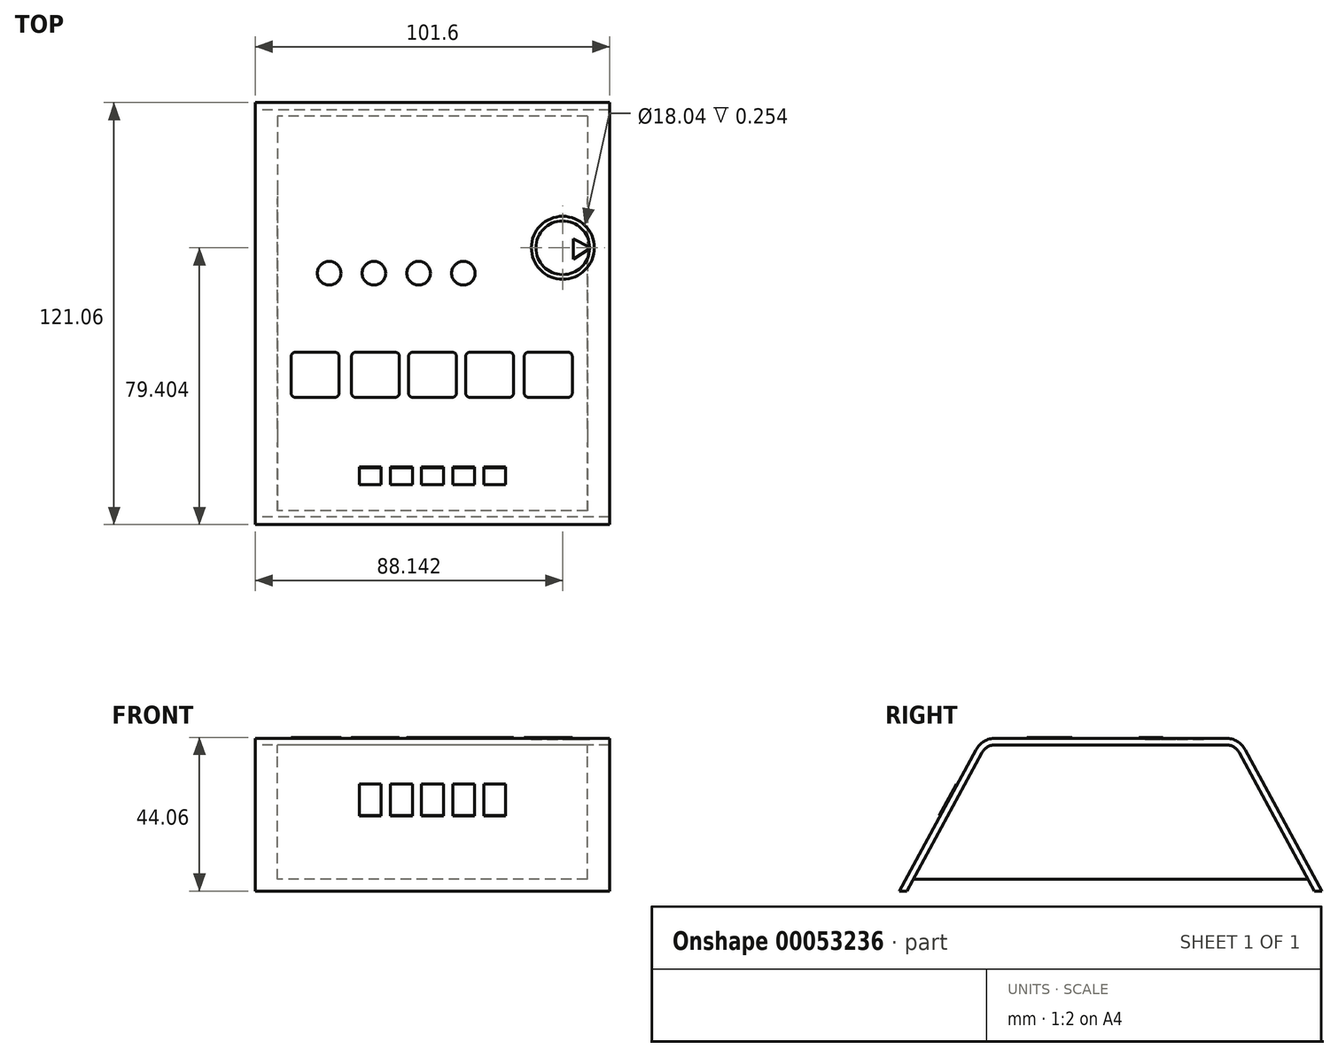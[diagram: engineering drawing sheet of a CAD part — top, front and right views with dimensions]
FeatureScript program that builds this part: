
annotation { "Feature Type Name" : "Feature", "Feature Type Description" : "" }
export const myFeature = defineFeature(function(context is Context, id is Id, definition is map)
    precondition{}
    {
        {
            var Q0;
            Q0=qCreatedBy(makeId("Top.planeOp"),FACE);
            var sketch = newSketch(context, id + "F0", { "sketchPlane" : qUnion([Q0])});
            skLineSegment(sketch, "E0.bottom", {"start": v(-38, 33) * mm, "end": v(38, 33) * mm});
            skLineSegment(sketch, "E0.top", {"start": v(-38, -33) * mm, "end": v(38, -33) * mm});
            skLineSegment(sketch, "E0.left", {"start": v(-38, 33) * mm, "end": v(-38, -33) * mm});
            skLineSegment(sketch, "E0.right", {"start": v(38, 33) * mm, "end": v(38, -33) * mm});
            skLineSegment(sketch, "E1", {"start": v(0, 33) * mm, "end": v(0, -33) * mm, "construction": true});
            skLineSegment(sketch, "E2", {"start": v(-38, 0) * mm, "end": v(38, 0) * mm, "construction": true});
            skSolve(sketch);
        }
        {
            var Q0;
            Q0=qCreatedBy(makeId("Right.planeOp"),FACE);
            var sketch = newSketch(context, id + "F1", { "sketchPlane" : qUnion([Q0])});
            skLineSegment(sketch, "E3", {"start": v(-60.53, -28.5) * mm, "end": v(-38.6, 11.98) * mm});
            skLineSegment(sketch, "E4", {"start": v(-33.02, 15.3) * mm, "end": v(0, 15.3) * mm});
            skPoint(sketch, "E5.visualSharp", {"position": v(-36.8, 15.3) * mm});
            skArc(sketch, "E5.filletArc", {"start": v(-33.02, 15.3) * mm, "mid": v(-36.27, 14.41) * mm, "end": v(-38.6, 11.98) * mm});
            skLineSegment(sketch, "E6.0", {"start": v(-33.02, 13.42) * mm, "end": v(7.41, 13.42) * mm});
            skArc(sketch, "E6.1", {"start": v(-33.02, 13.42) * mm, "mid": v(-35.3, 12.8) * mm, "end": v(-36.95, 11.08) * mm});
            skLineSegment(sketch, "E6.2", {"start": v(-58.39, -28.5) * mm, "end": v(-36.95, 11.08) * mm});
            skLineSegment(sketch, "E7", {"start": v(-60.53, -28.5) * mm, "end": v(-58.39, -28.5) * mm});
            skLineSegment(sketch, "E8.MirrorCS", {"start": v(33.02, 15.3) * mm, "end": v(0, 15.3) * mm});
            skLineSegment(sketch, "E9.MirrorCS", {"start": v(33.02, 13.42) * mm, "end": v(-7.41, 13.42) * mm});
            skArc(sketch, "E10.MirrorCS", {"start": v(33.02, 13.42) * mm, "mid": v(35.3, 12.8) * mm, "end": v(36.95, 11.08) * mm});
            skArc(sketch, "E11.MirrorCS", {"start": v(33.02, 15.3) * mm, "mid": v(36.27, 14.41) * mm, "end": v(38.6, 11.98) * mm});
            skLineSegment(sketch, "E12.MirrorCS", {"start": v(60.53, -28.5) * mm, "end": v(38.6, 11.98) * mm});
            skLineSegment(sketch, "E13.MirrorCS", {"start": v(58.39, -28.5) * mm, "end": v(36.95, 11.08) * mm});
            skLineSegment(sketch, "E14.MirrorCS", {"start": v(60.53, -28.5) * mm, "end": v(58.39, -28.5) * mm});
            skSolve(sketch);
        }
        {
            var Q0;
            Q0=makeQuery(id+"F1.imprint","IMPRINT",FACE,{"disambiguationData":[TD([[makeQuery(id+"F1.imprint","IMPRINT",EDGE,{"derivedFrom":sQuery(id+"F1.wireOp",EDGE,"E3")}),-1.0]])]});
            extrude(context, id + "F2", {"entities" : qUnion([Q0]), "endBound" : BoundingType.SYMMETRIC, "depth" : 101.6 * mm});
        }
        {
            var Q0;
            Q0 = qConstructionFilter(qBodyType(qCreatedBy(id + "F0" ,EDGE), BodyType.WIRE), ConstructionObject.NO);
            extrude(context, id + "F3", {"bodyType" : ToolBodyType.SURFACE, "surfaceEntities" : qUnion([Q0]), "oppositeDirection" : true, "depth" : 19 * mm});
        }
        {
            var Q0;
            Q0=makeQuery(id+"F2.opExtrude","SWEPT_FACE",FACE,{"disambiguationData":[OSD([sQuery(id+"F1.wireOp",EDGE,"E3")])]});
            var sketch = newSketch(context, id + "F4", { "sketchPlane" : qUnion([Q0])});
            skLineSegment(sketch, "E15.bottom", {"start": v(-21, -19.14) * mm, "end": v(-14.72, -19.14) * mm});
            skLineSegment(sketch, "E15.top", {"start": v(-21, -29.42) * mm, "end": v(-14.72, -29.42) * mm});
            skLineSegment(sketch, "E15.left", {"start": v(-21, -19.14) * mm, "end": v(-21, -29.42) * mm});
            skLineSegment(sketch, "E15.right", {"start": v(-14.72, -19.14) * mm, "end": v(-14.72, -29.42) * mm});
            skLineSegment(sketch, "E16.bottom", {"start": v(-12.07, -19.14) * mm, "end": v(-5.79, -19.14) * mm});
            skLineSegment(sketch, "E16.top", {"start": v(-12.07, -29.42) * mm, "end": v(-5.79, -29.42) * mm});
            skLineSegment(sketch, "E16.left", {"start": v(-12.07, -19.14) * mm, "end": v(-12.07, -29.42) * mm});
            skLineSegment(sketch, "E16.right", {"start": v(-5.79, -19.14) * mm, "end": v(-5.79, -29.42) * mm});
            skLineSegment(sketch, "E17.bottom", {"start": v(-3.14, -19.14) * mm, "end": v(3.14, -19.14) * mm});
            skLineSegment(sketch, "E17.top", {"start": v(-3.14, -29.42) * mm, "end": v(3.14, -29.42) * mm});
            skLineSegment(sketch, "E17.left", {"start": v(-3.14, -19.14) * mm, "end": v(-3.14, -29.42) * mm});
            skLineSegment(sketch, "E17.right", {"start": v(3.14, -19.14) * mm, "end": v(3.14, -29.42) * mm});
            skLineSegment(sketch, "E18.bottom", {"start": v(5.79, -19.14) * mm, "end": v(12.07, -19.14) * mm});
            skLineSegment(sketch, "E18.top", {"start": v(5.79, -29.42) * mm, "end": v(12.07, -29.42) * mm});
            skLineSegment(sketch, "E18.left", {"start": v(5.79, -19.14) * mm, "end": v(5.79, -29.42) * mm});
            skLineSegment(sketch, "E18.right", {"start": v(12.07, -19.14) * mm, "end": v(12.07, -29.42) * mm});
            skLineSegment(sketch, "E19.bottom", {"start": v(14.72, -19.14) * mm, "end": v(21, -19.14) * mm});
            skLineSegment(sketch, "E19.top", {"start": v(14.72, -29.42) * mm, "end": v(21, -29.42) * mm});
            skLineSegment(sketch, "E19.left", {"start": v(14.72, -19.14) * mm, "end": v(14.72, -29.42) * mm});
            skLineSegment(sketch, "E19.right", {"start": v(21, -19.14) * mm, "end": v(21, -29.42) * mm});
            skLineSegment(sketch, "E20", {"start": v(-14.72, -19.14) * mm, "end": v(-12.07, -19.14) * mm, "construction": true});
            skLineSegment(sketch, "E21", {"start": v(-5.79, -19.14) * mm, "end": v(-3.14, -19.14) * mm, "construction": true});
            skLineSegment(sketch, "E22", {"start": v(3.14, -19.14) * mm, "end": v(5.79, -19.14) * mm, "construction": true});
            skLineSegment(sketch, "E23", {"start": v(12.07, -19.14) * mm, "end": v(14.72, -19.14) * mm, "construction": true});
            skLineSegment(sketch, "E24", {"start": v(0, -19.14) * mm, "end": v(0, -29.42) * mm, "construction": true});
            skSolve(sketch);
        }
        {
            var Q0;
            Q0=makeQuery(id+"F4.imprint","IMPRINT",FACE,{"disambiguationData":[TD([[makeQuery(id+"F4.imprint","IMPRINT",EDGE,{"derivedFrom":sQuery(id+"F4.wireOp",EDGE,"E15.bottom")}),-1.0]])]});
            var Q1;
            Q1=makeQuery(id+"F4.imprint","IMPRINT",FACE,{"disambiguationData":[TD([[makeQuery(id+"F4.imprint","IMPRINT",EDGE,{"derivedFrom":sQuery(id+"F4.wireOp",EDGE,"E16.bottom")}),-1.0]])]});
            var Q2;
            Q2=makeQuery(id+"F4.imprint","IMPRINT",FACE,{"disambiguationData":[TD([[makeQuery(id+"F4.imprint","IMPRINT",EDGE,{"derivedFrom":sQuery(id+"F4.wireOp",EDGE,"E17.bottom")}),-1.0]])]});
            var Q3;
            Q3=makeQuery(id+"F4.imprint","IMPRINT",FACE,{"disambiguationData":[TD([[makeQuery(id+"F4.imprint","IMPRINT",EDGE,{"derivedFrom":sQuery(id+"F4.wireOp",EDGE,"E18.bottom")}),-1.0]])]});
            var Q4;
            Q4=makeQuery(id+"F4.imprint","IMPRINT",FACE,{"disambiguationData":[TD([[makeQuery(id+"F4.imprint","IMPRINT",EDGE,{"derivedFrom":sQuery(id+"F4.wireOp",EDGE,"E19.bottom")}),-1.0]])]});
            extrude(context, id + "F5", {"entities" : qUnion([Q0, Q1, Q2, Q3, Q4]), "operationType" : NewBodyOperationType.ADD, "depth" : 0.25 * mm});
        }
        {
            var Q0;
            Q0=makeQuery(id+"F2.opExtrude","SWEPT_FACE",FACE,{"disambiguationData":[OSD([sQuery(id+"F1.wireOp",EDGE,"E4"),sQuery(id+"F1.wireOp",EDGE,"E8.MirrorCS")])]});
            var sketch = newSketch(context, id + "F6", { "sketchPlane" : qUnion([Q0])});
            skLineSegment(sketch, "E25.bottom", {"start": v(-39.26, -11.05) * mm, "end": v(-28.05, -11.05) * mm});
            skLineSegment(sketch, "E25.top", {"start": v(-39.26, -24.05) * mm, "end": v(-28.05, -24.05) * mm});
            skLineSegment(sketch, "E25.left", {"start": v(-40.53, -12.32) * mm, "end": v(-40.53, -22.78) * mm});
            skLineSegment(sketch, "E25.right", {"start": v(-26.78, -12.32) * mm, "end": v(-26.78, -22.78) * mm});
            skLineSegment(sketch, "E26.bottom", {"start": v(-21.98, -11.05) * mm, "end": v(-10.77, -11.05) * mm});
            skLineSegment(sketch, "E26.top", {"start": v(-21.98, -24.05) * mm, "end": v(-10.77, -24.05) * mm});
            skLineSegment(sketch, "E26.left", {"start": v(-23.25, -12.32) * mm, "end": v(-23.25, -22.78) * mm});
            skLineSegment(sketch, "E26.right", {"start": v(-9.5, -12.32) * mm, "end": v(-9.5, -22.78) * mm});
            skLineSegment(sketch, "E27.bottom", {"start": v(-5.6, -11.05) * mm, "end": v(5.6, -11.05) * mm});
            skLineSegment(sketch, "E27.top", {"start": v(-5.6, -24.05) * mm, "end": v(5.6, -24.05) * mm});
            skLineSegment(sketch, "E27.left", {"start": v(6.87, -12.32) * mm, "end": v(6.87, -22.78) * mm});
            skLineSegment(sketch, "E27.right", {"start": v(-6.87, -12.32) * mm, "end": v(-6.87, -22.78) * mm});
            skLineSegment(sketch, "E28.bottom", {"start": v(10.77, -11.05) * mm, "end": v(21.98, -11.05) * mm});
            skLineSegment(sketch, "E28.top", {"start": v(10.77, -24.05) * mm, "end": v(21.98, -24.05) * mm});
            skLineSegment(sketch, "E28.left", {"start": v(9.5, -12.32) * mm, "end": v(9.5, -22.78) * mm});
            skLineSegment(sketch, "E28.right", {"start": v(23.25, -12.32) * mm, "end": v(23.25, -22.78) * mm});
            skLineSegment(sketch, "E29.bottom", {"start": v(27.58, -11.05) * mm, "end": v(38.79, -11.05) * mm});
            skLineSegment(sketch, "E29.top", {"start": v(27.58, -24.05) * mm, "end": v(38.79, -24.05) * mm});
            skLineSegment(sketch, "E29.left", {"start": v(26.31, -12.32) * mm, "end": v(26.31, -22.78) * mm});
            skLineSegment(sketch, "E29.right", {"start": v(40.06, -12.32) * mm, "end": v(40.06, -22.78) * mm});
            skLineSegment(sketch, "E30", {"start": v(-9.5, -11.05) * mm, "end": v(6.87, -11.05) * mm, "construction": true});
            skLineSegment(sketch, "E31", {"start": v(-6.87, -11.05) * mm, "end": v(9.5, -11.05) * mm, "construction": true});
            skLineSegment(sketch, "E32", {"start": v(0, -11.05) * mm, "end": v(0, -24.05) * mm, "construction": true});
            skPoint(sketch, "E33.visualSharp", {"position": v(-40.53, -11.05) * mm});
            skArc(sketch, "E33.filletArc", {"start": v(-39.26, -11.05) * mm, "mid": v(-40.16, -11.43) * mm, "end": v(-40.53, -12.32) * mm});
            skPoint(sketch, "E34.visualSharp", {"position": v(-26.78, -11.05) * mm});
            skArc(sketch, "E34.filletArc", {"start": v(-26.78, -12.32) * mm, "mid": v(-27.15, -11.43) * mm, "end": v(-28.05, -11.05) * mm});
            skPoint(sketch, "E35.visualSharp", {"position": v(-26.78, -24.05) * mm});
            skArc(sketch, "E35.filletArc", {"start": v(-28.05, -24.05) * mm, "mid": v(-27.15, -23.68) * mm, "end": v(-26.78, -22.78) * mm});
            skPoint(sketch, "E36.visualSharp", {"position": v(-40.53, -24.05) * mm});
            skArc(sketch, "E36.filletArc", {"start": v(-40.53, -22.78) * mm, "mid": v(-40.16, -23.68) * mm, "end": v(-39.26, -24.05) * mm});
            skPoint(sketch, "E37.visualSharp", {"position": v(-23.25, -11.05) * mm});
            skArc(sketch, "E37.filletArc", {"start": v(-21.98, -11.05) * mm, "mid": v(-22.87, -11.43) * mm, "end": v(-23.25, -12.32) * mm});
            skPoint(sketch, "E38.visualSharp", {"position": v(-9.5, -11.05) * mm});
            skArc(sketch, "E38.filletArc", {"start": v(-9.5, -12.32) * mm, "mid": v(-9.87, -11.43) * mm, "end": v(-10.77, -11.05) * mm});
            skPoint(sketch, "E39.visualSharp", {"position": v(-9.5, -24.05) * mm});
            skArc(sketch, "E39.filletArc", {"start": v(-10.77, -24.05) * mm, "mid": v(-9.87, -23.68) * mm, "end": v(-9.5, -22.78) * mm});
            skPoint(sketch, "E40.visualSharp", {"position": v(-23.25, -24.05) * mm});
            skArc(sketch, "E40.filletArc", {"start": v(-23.25, -22.78) * mm, "mid": v(-22.87, -23.68) * mm, "end": v(-21.98, -24.05) * mm});
            skPoint(sketch, "E41.visualSharp", {"position": v(-6.87, -11.05) * mm});
            skArc(sketch, "E41.filletArc", {"start": v(-5.6, -11.05) * mm, "mid": v(-6.5, -11.43) * mm, "end": v(-6.87, -12.32) * mm});
            skPoint(sketch, "E42.visualSharp", {"position": v(6.87, -11.05) * mm});
            skArc(sketch, "E42.filletArc", {"start": v(6.87, -12.32) * mm, "mid": v(6.5, -11.43) * mm, "end": v(5.6, -11.05) * mm});
            skPoint(sketch, "E43.visualSharp", {"position": v(6.87, -24.05) * mm});
            skArc(sketch, "E43.filletArc", {"start": v(5.6, -24.05) * mm, "mid": v(6.5, -23.68) * mm, "end": v(6.87, -22.78) * mm});
            skPoint(sketch, "E44.visualSharp", {"position": v(-6.87, -24.05) * mm});
            skArc(sketch, "E44.filletArc", {"start": v(-6.87, -22.78) * mm, "mid": v(-6.5, -23.68) * mm, "end": v(-5.6, -24.05) * mm});
            skPoint(sketch, "E45.visualSharp", {"position": v(9.5, -11.05) * mm});
            skArc(sketch, "E45.filletArc", {"start": v(10.77, -11.05) * mm, "mid": v(9.87, -11.43) * mm, "end": v(9.5, -12.32) * mm});
            skPoint(sketch, "E46.visualSharp", {"position": v(23.25, -11.05) * mm});
            skArc(sketch, "E46.filletArc", {"start": v(23.25, -12.32) * mm, "mid": v(22.87, -11.43) * mm, "end": v(21.98, -11.05) * mm});
            skPoint(sketch, "E47.visualSharp", {"position": v(23.25, -24.05) * mm});
            skArc(sketch, "E47.filletArc", {"start": v(21.98, -24.05) * mm, "mid": v(22.87, -23.68) * mm, "end": v(23.25, -22.78) * mm});
            skPoint(sketch, "E48.visualSharp", {"position": v(9.5, -24.05) * mm});
            skArc(sketch, "E48.filletArc", {"start": v(9.5, -22.78) * mm, "mid": v(9.87, -23.68) * mm, "end": v(10.77, -24.05) * mm});
            skPoint(sketch, "E49.visualSharp", {"position": v(26.31, -11.05) * mm});
            skArc(sketch, "E49.filletArc", {"start": v(27.58, -11.05) * mm, "mid": v(26.68, -11.43) * mm, "end": v(26.31, -12.32) * mm});
            skPoint(sketch, "E50.visualSharp", {"position": v(40.06, -11.05) * mm});
            skArc(sketch, "E50.filletArc", {"start": v(40.06, -12.32) * mm, "mid": v(39.69, -11.43) * mm, "end": v(38.79, -11.05) * mm});
            skPoint(sketch, "E51.visualSharp", {"position": v(40.06, -24.05) * mm});
            skArc(sketch, "E51.filletArc", {"start": v(38.79, -24.05) * mm, "mid": v(39.69, -23.68) * mm, "end": v(40.06, -22.78) * mm});
            skPoint(sketch, "E52.visualSharp", {"position": v(26.31, -24.05) * mm});
            skArc(sketch, "E52.filletArc", {"start": v(26.31, -22.78) * mm, "mid": v(26.68, -23.68) * mm, "end": v(27.58, -24.05) * mm});
            skSolve(sketch);
        }
        {
            var Q0;
            Q0 = qSketchRegion(id + "F6", true);
            extrude(context, id + "F7", {"entities" : qUnion([Q0]), "operationType" : NewBodyOperationType.ADD, "depth" : 0.25 * mm});
        }
        {
            var Q0;
            Q0=qCreatedBy(makeId("Right.planeOp"),FACE);
            var sketch = newSketch(context, id + "F8", { "sketchPlane" : qUnion([Q0])});
            skLineSegment(sketch, "E53.0", {"start": v(-58.39, -28.5) * mm, "end": v(-36.95, 11.08) * mm});
            skArc(sketch, "E54.0", {"start": v(-33.02, 13.42) * mm, "mid": v(-35.3, 12.8) * mm, "end": v(-36.95, 11.08) * mm});
            skLineSegment(sketch, "E54.1", {"start": v(-33.02, 13.42) * mm, "end": v(33.02, 13.42) * mm});
            skArc(sketch, "E54.2", {"start": v(33.02, 13.42) * mm, "mid": v(35.3, 12.8) * mm, "end": v(36.95, 11.08) * mm});
            skLineSegment(sketch, "E54.3", {"start": v(58.39, -28.5) * mm, "end": v(36.95, 11.08) * mm});
            skLineSegment(sketch, "E55", {"start": v(56.6, -25.18) * mm, "end": v(-56.6, -25.18) * mm});
            skSolve(sketch);
        }
        {
            var Q0;
            Q0 = qSketchRegion(id + "F8", true);
            extrude(context, id + "F9", {"entities" : qUnion([Q0]), "endBound" : BoundingType.SYMMETRIC, "depth" : 88.9 * mm});
        }
        {
            var Q0;
            Q0=makeQuery(id+"F2.opExtrude","SWEPT_FACE",FACE,{"disambiguationData":[OSD([sQuery(id+"F1.wireOp",EDGE,"E4"),sQuery(id+"F1.wireOp",EDGE,"E8.MirrorCS")])]});
            var sketch = newSketch(context, id + "F10", { "sketchPlane" : qUnion([Q0])});
            skCircle(sketch, "E56", {"center": v(-29.61, 11.57) * mm, "radius": 3.38 * mm});
            skCircle(sketch, "E57", {"center": v(-16.8, 11.57) * mm, "radius": 3.38 * mm});
            skCircle(sketch, "E58", {"center": v(-3.97, 11.57) * mm, "radius": 3.38 * mm});
            skCircle(sketch, "E59", {"center": v(8.85, 11.57) * mm, "radius": 3.38 * mm});
            skLineSegment(sketch, "E60", {"start": v(-29.61, 11.57) * mm, "end": v(-16.8, 11.57) * mm, "construction": true});
            skLineSegment(sketch, "E61", {"start": v(-16.8, 11.57) * mm, "end": v(-3.97, 11.57) * mm, "construction": true});
            skLineSegment(sketch, "E62", {"start": v(-3.97, 11.57) * mm, "end": v(8.85, 11.57) * mm, "construction": true});
            skSolve(sketch);
        }
        {
            var Q0;
            Q0 = qSketchRegion(id + "F10", true);
            extrude(context, id + "F11", {"entities" : qUnion([Q0]), "operationType" : NewBodyOperationType.ADD, "depth" : 0.25 * mm});
        }
        {
            var Q0;
            Q0=makeQuery(id+"F2.opExtrude","SWEPT_FACE",FACE,{"disambiguationData":[OSD([sQuery(id+"F1.wireOp",EDGE,"E4"),sQuery(id+"F1.wireOp",EDGE,"E8.MirrorCS")])]});
            var sketch = newSketch(context, id + "F12", { "sketchPlane" : qUnion([Q0])});
            skCircle(sketch, "E63", {"center": v(37.34, 18.87) * mm, "radius": 7.7 * mm});
            skLineSegment(sketch, "E64", {"start": v(40.32, 21.44) * mm, "end": v(40.32, 15.55) * mm});
            skCircle(sketch, "E65", {"center": v(37.34, 18.87) * mm, "radius": 9.02 * mm});
            skLineSegment(sketch, "E66", {"start": v(40.32, 21.44) * mm, "end": v(45.04, 19.06) * mm});
            skLineSegment(sketch, "E67", {"start": v(40.32, 15.55) * mm, "end": v(45.04, 18.69) * mm});
            skSolve(sketch);
        }
        {
            var Q0;
            Q0 = qSketchRegion(id + "F12", true);
            var Q1;
            Q1=makeQuery(id+"F12.imprint","IMPRINT",FACE,{"disambiguationData":[TD([[makeQuery(id+"F12.imprint","IMPRINT",EDGE,{"derivedFrom":sQuery(id+"F12.wireOp",EDGE,"8422e89c-0de3-4bcb-b7f2-480c3dd7b818")}),1.0]])]});
            var Q2;
            Q2=makeQuery(id+"F12.imprint","IMPRINT",FACE,{"disambiguationData":[TD([[makeQuery(id+"F12.imprint","IMPRINT",EDGE,{"derivedFrom":sQuery(id+"F12.wireOp",EDGE,"E64")}),1.0]])]});
            extrude(context, id + "F13", {"entities" : qUnion([Q0, Q1, Q2]), "operationType" : NewBodyOperationType.REMOVE, "oppositeDirection" : true, "depth" : 0.25 * mm});
        }
    });
